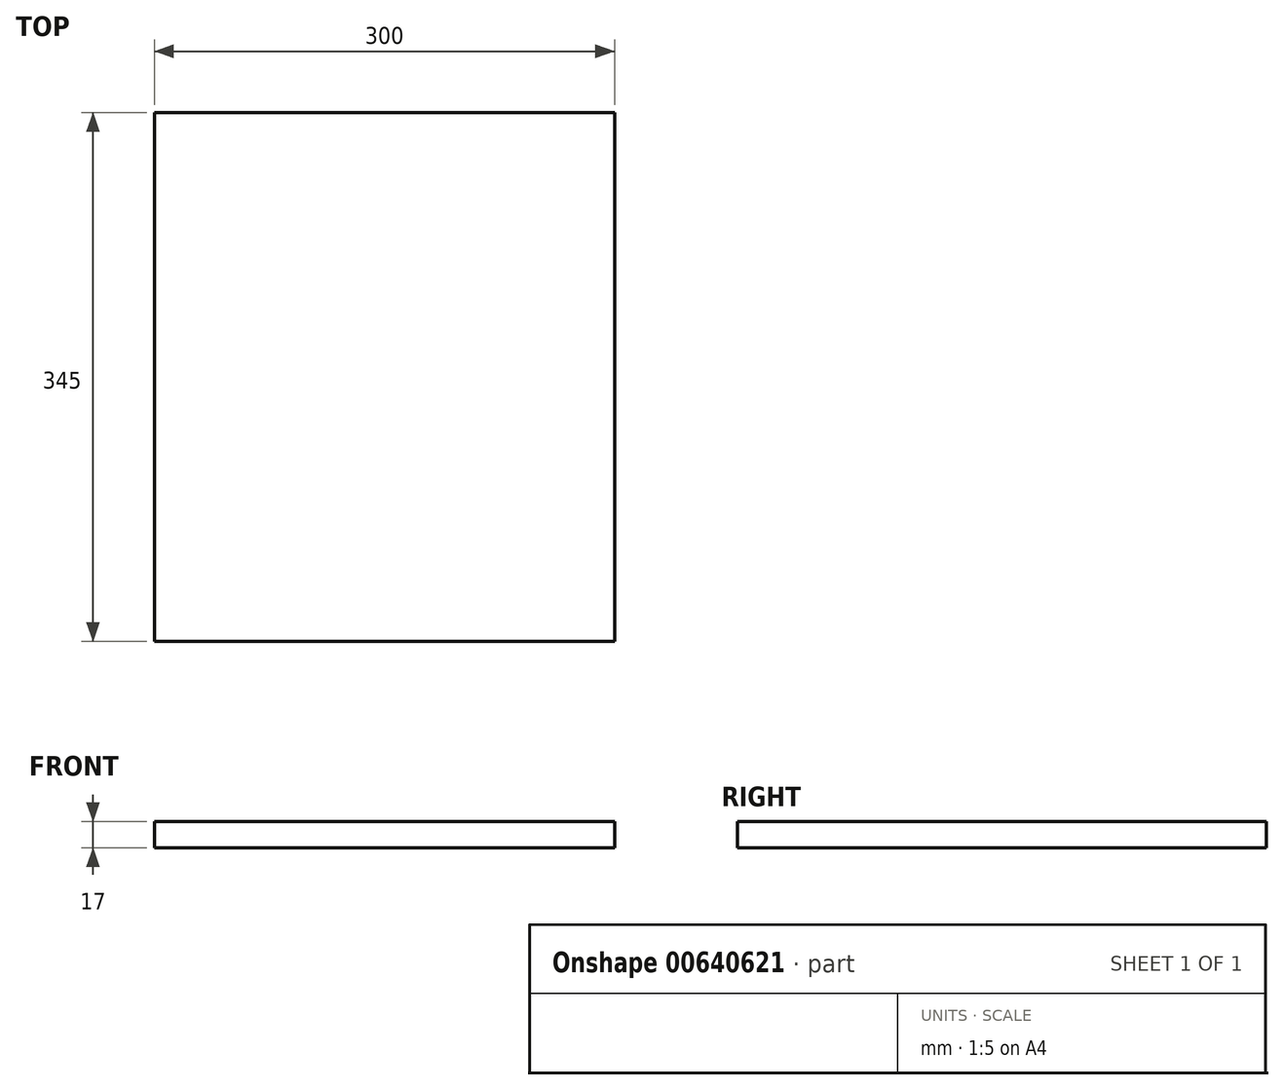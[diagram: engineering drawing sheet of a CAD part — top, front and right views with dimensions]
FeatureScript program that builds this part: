
annotation { "Feature Type Name" : "Feature", "Feature Type Description" : "" }
export const myFeature = defineFeature(function(context is Context, id is Id, definition is map)
    precondition{}
    {
        {
            var Q0;
            Q0=qCreatedBy(makeId("Top.planeOp"),FACE);
            var sketch = newSketch(context, id + "F0", { "sketchPlane" : qUnion([Q0])});
            skLineSegment(sketch, "E0.bottom", {"start": v(0, 0) * mm, "end": v(-300, 0) * mm});
            skLineSegment(sketch, "E0.top", {"start": v(0, 345) * mm, "end": v(-300, 345) * mm});
            skLineSegment(sketch, "E0.left", {"start": v(0, 0) * mm, "end": v(0, 345) * mm});
            skLineSegment(sketch, "E0.right", {"start": v(-300, 0) * mm, "end": v(-300, 345) * mm});
            skSolve(sketch);
        }
        {
            var Q0;
            Q0=makeQuery(id+"F0.imprint","IMPRINT",FACE,{"disambiguationData":[TD([[makeQuery(id+"F0.imprint","IMPRINT",EDGE,{"derivedFrom":sQuery(id+"F0.wireOp",EDGE,"E0.bottom")}),-1.0]])]});
            extrude(context, id + "F1", {"entities" : qUnion([Q0]), "depth" : 17 * mm, "offsetDistance" : 25 * mm});
        }
    });
